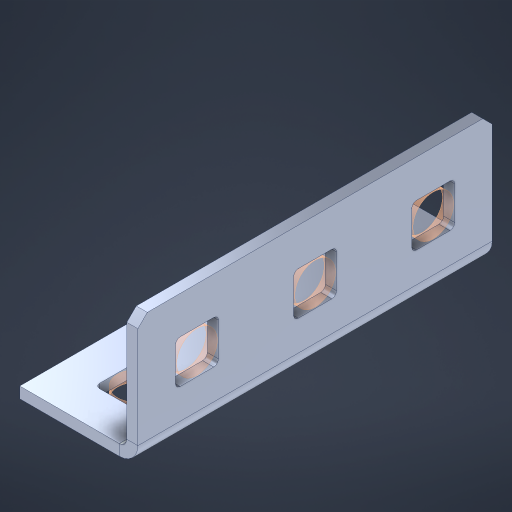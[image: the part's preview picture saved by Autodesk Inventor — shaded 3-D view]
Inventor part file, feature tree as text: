
AUTODESK INVENTOR PART (.ipt)
format: ipt  version: 2023 (Build 270158000, 158)  size: 400,384 bytes
history: native  units: in
note: dims shown in document units (in); Inventor stores cm internally (conversion verified against a paired STEP export)
features: other x11, sheet_metal_op x10, sketch x8, extrude x5, mirror x1, pattern_linear x1, chamfer x1
ambient origin geometry x8: Origin, YZ Plane, XZ Plane, XY Plane, X Axis, Y Axis, Z Axis, Center Point
bodies: Solid1 (feature_tree), Body (feature_tree)
feature tree (37):
  other  "Flange Pattern Plane"
  sheet_metal_op  "Flange Pattern"
  sheet_metal_op  "Body Pattern"
  other  "Arc Length"
  mirror  "Notch Mirror"
  pattern_linear  "Notch Pattern"  Spacing1=0.1875in  [1 undecoded]
  chamfer  "End Chamfer"
  extrude  "Half Cut"  Depth=0.0469in
  sketch  "Sketch1"  dims[d0=2.5in]
  other  "Plate1"
  sketch  "Sketch2"  dims[d1=1.5in]
  other  "Plate2"
  sheet_metal_op  "Bend1"
  sheet_metal_op  "Corner1"
  sketch  "Sketch3"  dims[d2=0.0469in]
  other  "Flange Pattern Sketch"
  sketch  "Sketch7"  dims[d3=0.0469in]
  other  "Srf1"
  other  "Srf2"
  sketch  "Sketch8"  dims[d4=0.0234in]
  sketch  "Sketch9"  dims[d5=0.0938in]
  other  "Srf91"
  sheet_metal_op  "Body Pattern Sketch"
  other  "Srf92"
  sketch  "Sketch13"  dims[d6=0.0469in]
  sketch  "Sketch14"  dims[d7=0.5in d8=90.0deg d9=0.0312in d10=0.1875in d11=0.0469in d12=0.0469in d16=0.182in d17=0.02in d18=0.0469in d19=0.0in d20=0.25in d21=0.25in d46=0.172in d47=1.0in d48=0.0in d49=0.182in d50=0.02in d51=0.25in d52=0.25in d53=0.0469in d54=0.0in d55=0.172in d56=1.0in d57=0.0in d60=1.1811in d62=0.5in d63=0.3937in d65=0.5in d85=0.1227in d86=0.1659in d88=0.04in d89=0.0469in d90=0.0in d91=0.04in d92=0.0491in d95=2.5in d96=0.04in d97=0.25in d98=45.0deg d101=0.0in d102=2.497in d131=0.5in d132=1.1811in d134=0.5in d139=0.5in]
  other  "Srf856"
  other  "Srf1310"
  sheet_metal_op  "Flange Stamp"
  sheet_metal_op  "Flange Circle"
  sheet_metal_op  "Body Stamp"
  sheet_metal_op  "Body Circle"
  sheet_metal_op  "Notch"
  extrude  "ExtrusionSrf2"  Depth=0.0469in
  extrude  "ExtrusionSrf92"  Depth=0.182in
  extrude  "ExtrusionSrf856"  Depth=0.02in
  extrude  "ExtrusionSrf1310"  Depth=0.0469in
note: 1 required parameter value undecoded (feature->parameter linkage not recoverable at this tier; creation-order binding heuristic only, values carry confidence <= 0.55)
